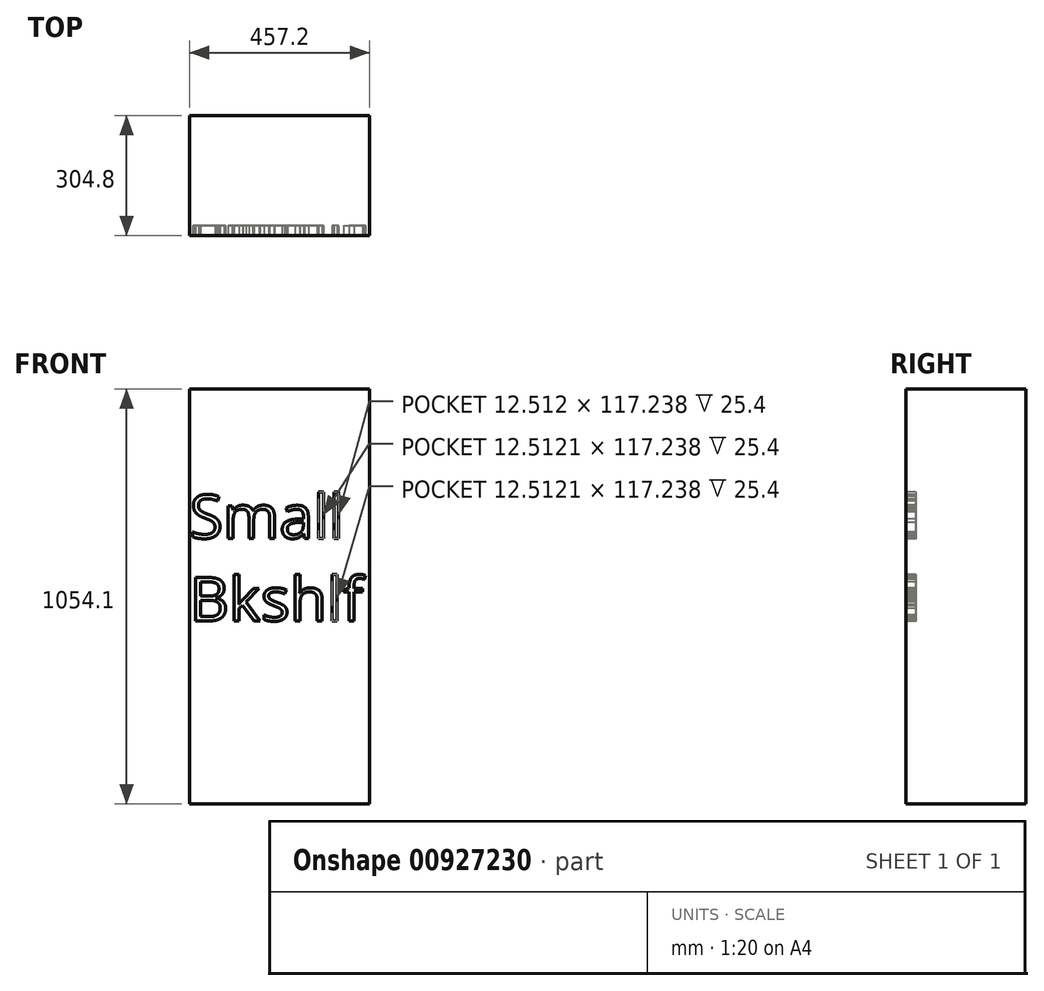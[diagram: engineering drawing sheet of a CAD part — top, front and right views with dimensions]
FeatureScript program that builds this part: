
annotation { "Feature Type Name" : "Feature", "Feature Type Description" : "" }
export const myFeature = defineFeature(function(context is Context, id is Id, definition is map)
    precondition{}
    {
        {
            var Q0;
            Q0=qCreatedBy(makeId("Front.planeOp"),FACE);
            var sketch = newSketch(context, id + "F0", { "sketchPlane" : qUnion([Q0])});
            skLineSegment(sketch, "E0.bottom", {"start": v(228.6, -527.05) * mm, "end": v(-228.6, -527.05) * mm});
            skLineSegment(sketch, "E0.top", {"start": v(228.6, 527.05) * mm, "end": v(-228.6, 527.05) * mm});
            skLineSegment(sketch, "E0.left", {"start": v(228.6, -527.05) * mm, "end": v(228.6, 527.05) * mm});
            skLineSegment(sketch, "E0.right", {"start": v(-228.6, -527.05) * mm, "end": v(-228.6, 527.05) * mm});
            skPoint(sketch, "E0.middle", {"position": v(0, 0) * mm});
            skSolve(sketch);
        }
        {
            var Q0;
            Q0 = qSketchRegion(id + "F0", true);
            extrude(context, id + "F1", {"entities" : qUnion([Q0]), "endBound" : BoundingType.SYMMETRIC, "depth" : 304.8 * mm, "offsetDistance" : 25.4 * mm});
        }
        {
            var Q0;
            Q0=makeQuery(id+"F1.opExtrude","CAP_FACE",FACE,{"disambiguationData":[OSD([sQuery(id+"F0.wireOp",EDGE,"E0.bottom"),sQuery(id+"F0.wireOp",EDGE,"E0.top"),sQuery(id+"F0.wireOp",EDGE,"E0.left"),sQuery(id+"F0.wireOp",EDGE,"E0.right")])],"isStart":false});
            var sketch = newSketch(context, id + "F2", { "sketchPlane" : qUnion([Q0])});
            skText(sketch, "E1", { "text": "Small\nBkshlf", "fontName": "OpenSans-Regular.ttf"});
            const initialGuessF2  = {"E1": [-0.2286, 0.14798, 1, 0, 0.11109]};
            skSetInitialGuess(sketch, initialGuessF2);
            skSolve(sketch);
        }
        {
            var Q0;
            Q0 = qSketchRegion(id + "F2", true);
            extrude(context, id + "F3", {"entities" : qUnion([Q0]), "operationType" : NewBodyOperationType.REMOVE, "oppositeDirection" : true, "depth" : 25.4 * mm, "offsetDistance" : 25.4 * mm});
        }
    });
